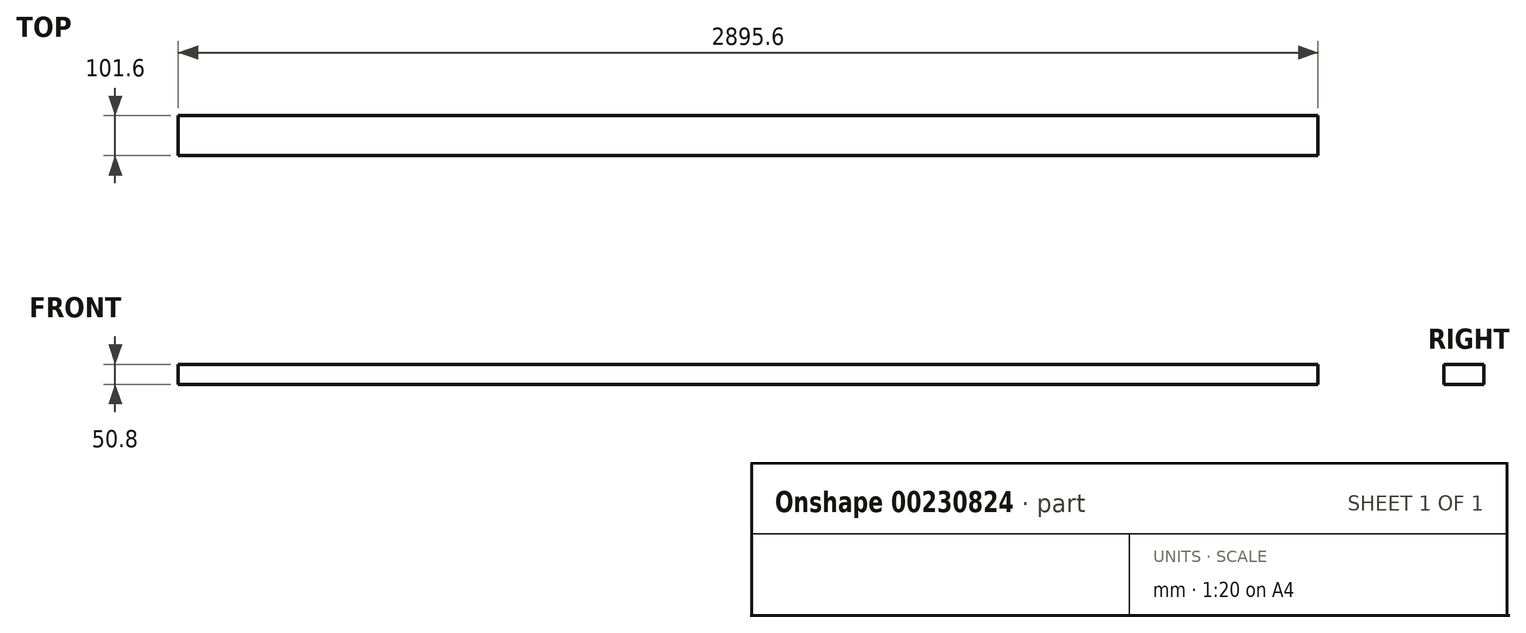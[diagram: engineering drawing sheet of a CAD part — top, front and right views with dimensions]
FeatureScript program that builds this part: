
annotation { "Feature Type Name" : "Feature", "Feature Type Description" : "" }
export const myFeature = defineFeature(function(context is Context, id is Id, definition is map)
    precondition{}
    {
        {
            var Q0;
            Q0=qCreatedBy(makeId("Top.planeOp"),FACE);
            var sketch = newSketch(context, id + "F0", { "sketchPlane" : qUnion([Q0])});
            skLineSegment(sketch, "E0.bottom", {"start": v(-1318.23, -93.78) * mm, "end": v(1577.37, -93.78) * mm});
            skLineSegment(sketch, "E0.top", {"start": v(-1318.23, -195.38) * mm, "end": v(1577.37, -195.38) * mm});
            skLineSegment(sketch, "E0.left", {"start": v(-1318.23, -93.78) * mm, "end": v(-1318.23, -195.38) * mm});
            skLineSegment(sketch, "E0.right", {"start": v(1577.37, -93.78) * mm, "end": v(1577.37, -195.38) * mm});
            skSolve(sketch);
        }
        {
            var Q0;
            Q0 = qSketchRegion(id + "F0", true);
            extrude(context, id + "F1", {"entities" : qUnion([Q0]), "depth" : 50.8 * mm});
        }
    });
